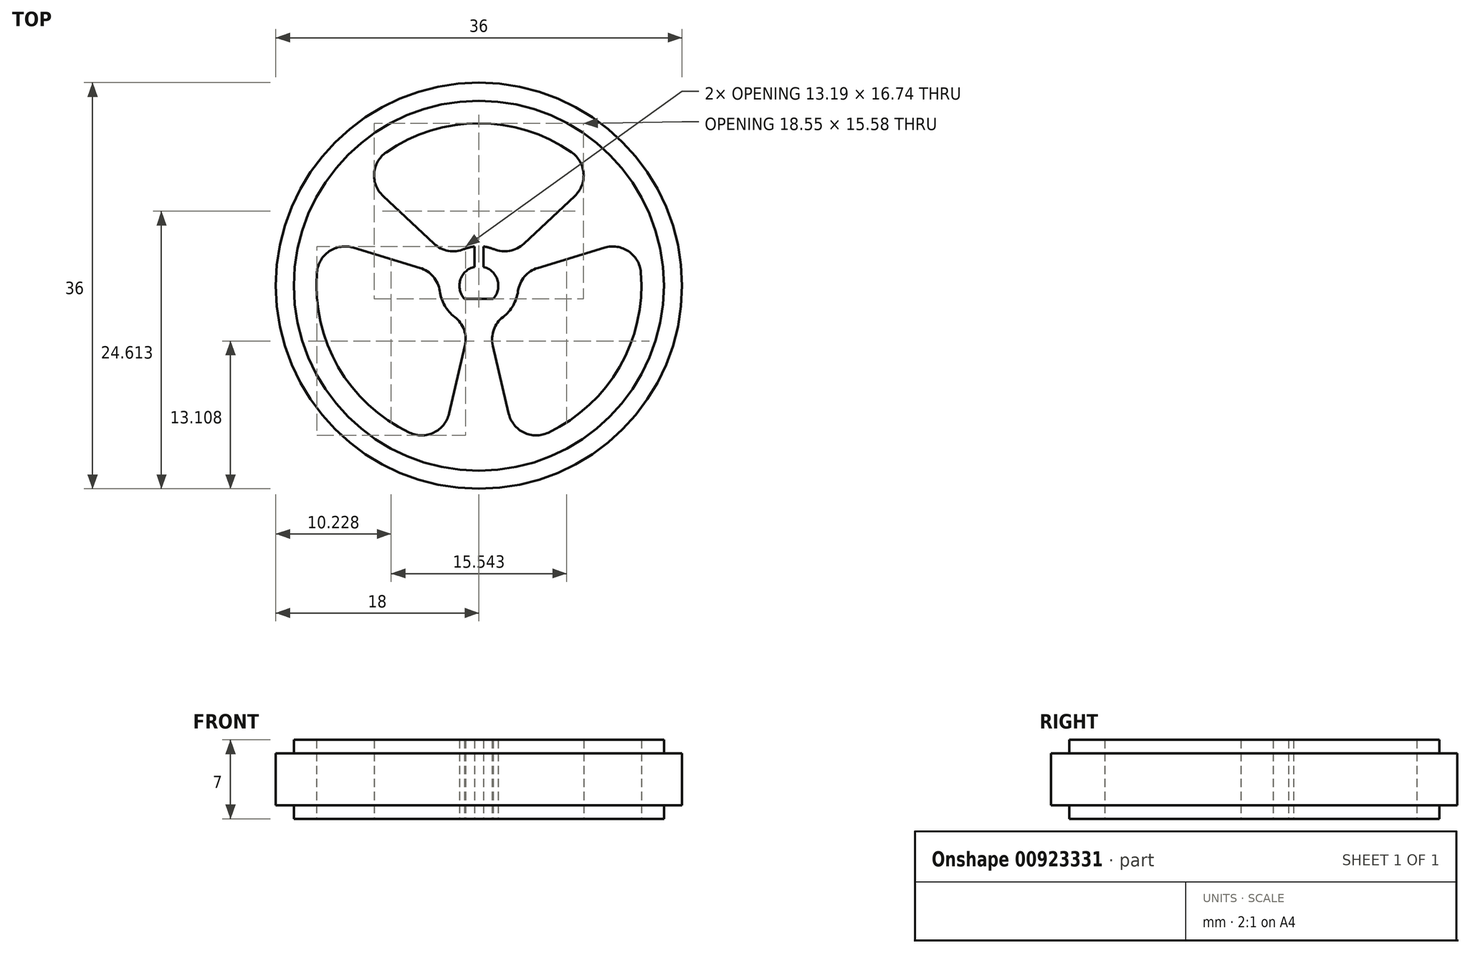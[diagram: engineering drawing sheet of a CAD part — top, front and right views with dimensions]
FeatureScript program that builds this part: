
annotation { "Feature Type Name" : "Feature", "Feature Type Description" : "" }
export const myFeature = defineFeature(function(context is Context, id is Id, definition is map)
    precondition{}
    {
        {
            var Q0;
            Q0=qCreatedBy(makeId("Front.planeOp"),FACE);
            var sketch = newSketch(context, id + "F0", { "sketchPlane" : qUnion([Q0])});
            skLineSegment(sketch, "E0", {"start": v(0, 0) * mm, "end": v(-16.4, 0) * mm});
            skLineSegment(sketch, "E1", {"start": v(-16.4, 0) * mm, "end": v(-16.4, 1.2) * mm});
            skLineSegment(sketch, "E2", {"start": v(-16.4, 1.2) * mm, "end": v(-18, 1.2) * mm});
            skLineSegment(sketch, "E3", {"start": v(-18, 1.2) * mm, "end": v(-18, 5.8) * mm});
            skLineSegment(sketch, "E4", {"start": v(-18, 5.8) * mm, "end": v(-16.4, 5.8) * mm});
            skLineSegment(sketch, "E5", {"start": v(-16.4, 5.8) * mm, "end": v(-16.4, 7) * mm});
            skLineSegment(sketch, "E6", {"start": v(-16.4, 7) * mm, "end": v(0, 7) * mm});
            skLineSegment(sketch, "E7", {"start": v(0, 7) * mm, "end": v(0, 0) * mm});
            skSolve(sketch);
        }
        {
            var Q0;
            Q0=makeQuery(id+"F0.imprint","IMPRINT",FACE,{"disambiguationData":[TD([[makeQuery(id+"F0.imprint","IMPRINT",EDGE,{"derivedFrom":sQuery(id+"F0.wireOp",EDGE,"E0")}),-1.0]])]});
            var Q1;
            Q1=sQuery(id+"F0.wireOp",EDGE,"E7");
            revolve(context, id + "F1", {"surfaceOperationType" : NewSurfaceOperationType.NEW, "entities" : qUnion([Q0]), "axis" : qUnion([Q1]), "revolveType" : RevolveType.FULL});
        }
        {
            var Q0;
            Q0=qCreatedBy(makeId("Top.planeOp"),FACE);
            var sketch = newSketch(context, id + "F2", { "sketchPlane" : qUnion([Q0])});
            skArc(sketch, "E8", {"start": v(-0.4, 1.68) * mm, "mid": v(0, -1.72) * mm, "end": v(0.4, 1.68) * mm});
            skLineSegment(sketch, "E9", {"start": v(-1.26, -1.17) * mm, "end": v(1.26, -1.17) * mm});
            skCircle(sketch, "E10.0", {"center": v(0, 0) * mm, "radius": 16.4 * mm});
            skCircle(sketch, "E11.0", {"center": v(0, 0) * mm, "radius": 14.4 * mm});
            skArc(sketch, "E12", {"start": v(-0.4, 3.48) * mm, "mid": v(0, -3.5) * mm, "end": v(0.4, 3.48) * mm});
            skLineSegment(sketch, "E13", {"start": v(-0.4, 1.68) * mm, "end": v(-0.4, 3.48) * mm});
            skLineSegment(sketch, "E14", {"start": v(0.4, 1.68) * mm, "end": v(0.4, 3.48) * mm});
            skLineSegment(sketch, "E15", {"start": v(-0.8, -3.4) * mm, "end": v(-3.27, -14.02) * mm});
            skLineSegment(sketch, "E16", {"start": v(0.8, -3.4) * mm, "end": v(3.27, -14.02) * mm});
            skLineSegment(sketch, "E17", {"start": v(0, -3.5) * mm, "end": v(0, -14.4) * mm, "construction": true});
            skLineSegment(sketch, "E18.1.0", {"start": v(3.35, 1.02) * mm, "end": v(13.78, 4.18) * mm});
            skLineSegment(sketch, "E18.1.1", {"start": v(2.55, 2.4) * mm, "end": v(10.51, 9.84) * mm});
            skLineSegment(sketch, "E18.2.0", {"start": v(-2.55, 2.4) * mm, "end": v(-10.51, 9.84) * mm});
            skLineSegment(sketch, "E18.2.1", {"start": v(-3.35, 1.02) * mm, "end": v(-13.78, 4.18) * mm});
            skSolve(sketch);
        }
        {
            var Q0;
            {var subQ5=sQuery(id+"F2.wireOp",EDGE,"E9");Q0=makeQuery(id+"F2.imprint","IMPRINT",FACE,{"disambiguationData":[TD([[makeQuery(id+"F2.imprint","IMPRINT",EDGE,{"derivedFrom":subQ5}),1.0]])]});}
            var Q1;
            {var subQ0=sQuery(id+"F2.wireOp",EDGE,"E16");Q1=makeQuery(id+"F2.imprint","IMPRINT",FACE,{"disambiguationData":[TD([[makeQuery(id+"F2.imprint","IMPRINT",EDGE,{"derivedFrom":subQ0}),1.0]])]});}
            var Q2;
            {var subQ0=sQuery(id+"F2.wireOp",EDGE,"E15");Q2=makeQuery(id+"F2.imprint","IMPRINT",FACE,{"disambiguationData":[TD([[makeQuery(id+"F2.imprint","IMPRINT",EDGE,{"derivedFrom":subQ0}),-1.0]])]});}
            var Q3;
            Q3=makeQuery(id+"F1.opRevolve","SWEPT_FACE",FACE,{"disambiguationData":[OSD([sQuery(id+"F0.wireOp",EDGE,"E6")])]});
            extrude(context, id + "F3", {"entities" : qUnion([Q0, Q1, Q2]), "operationType" : NewBodyOperationType.REMOVE, "endBound" : BoundingType.UP_TO_SURFACE, "depth" : 25 * mm, "endBoundEntityFace" : qUnion([Q3]), "offsetDistance" : 25 * mm});
        }
        {
            var Q0;
            Q0=makeQuery(id+"F3.boolean.opBoolean","COPY",EDGE,{"derivedFrom":makeQuery(id+"F3.opExtrude","SWEPT_EDGE",EDGE,{"disambiguationData":[OSD([sQuery(id+"F2.wireOp",EDGE,"E12"),sQuery(id+"F2.wireOp",EDGE,"E18.2.1")])]})});
            var Q1;
            Q1=makeQuery(id+"F3.boolean.opBoolean","COPY",EDGE,{"derivedFrom":makeQuery(id+"F3.opExtrude","SWEPT_EDGE",EDGE,{"disambiguationData":[OSD([sQuery(id+"F2.wireOp",EDGE,"E12"),sQuery(id+"F2.wireOp",EDGE,"E15")])]})});
            var Q2;
            Q2=makeQuery(id+"F3.boolean.opBoolean","COPY",EDGE,{"derivedFrom":makeQuery(id+"F3.opExtrude","SWEPT_EDGE",EDGE,{"disambiguationData":[OSD([sQuery(id+"F2.wireOp",EDGE,"E12"),sQuery(id+"F2.wireOp",EDGE,"E16")])]})});
            var Q3;
            Q3=makeQuery(id+"F3.boolean.opBoolean","COPY",EDGE,{"derivedFrom":makeQuery(id+"F3.opExtrude","SWEPT_EDGE",EDGE,{"disambiguationData":[OSD([sQuery(id+"F2.wireOp",EDGE,"E12"),sQuery(id+"F2.wireOp",EDGE,"E18.1.0")])]})});
            var Q4;
            Q4=makeQuery(id+"F3.boolean.opBoolean","COPY",EDGE,{"derivedFrom":makeQuery(id+"F3.opExtrude","SWEPT_EDGE",EDGE,{"disambiguationData":[OSD([sQuery(id+"F2.wireOp",EDGE,"E12"),sQuery(id+"F2.wireOp",EDGE,"E18.2.0")])]})});
            var Q5;
            Q5=makeQuery(id+"F3.boolean.opBoolean","COPY",EDGE,{"derivedFrom":makeQuery(id+"F3.opExtrude","SWEPT_EDGE",EDGE,{"disambiguationData":[OSD([sQuery(id+"F2.wireOp",EDGE,"E12"),sQuery(id+"F2.wireOp",EDGE,"E18.1.1")])]})});
            var Q6;
            Q6=makeQuery(id+"F3.boolean.opBoolean","COPY",EDGE,{"derivedFrom":makeQuery(id+"F3.opExtrude","SWEPT_EDGE",EDGE,{"disambiguationData":[OSD([sQuery(id+"F2.wireOp",EDGE,"E11.0"),sQuery(id+"F2.wireOp",EDGE,"E18.2.0")])]})});
            var Q7;
            Q7=makeQuery(id+"F3.boolean.opBoolean","COPY",EDGE,{"derivedFrom":makeQuery(id+"F3.opExtrude","SWEPT_EDGE",EDGE,{"disambiguationData":[OSD([sQuery(id+"F2.wireOp",EDGE,"E11.0"),sQuery(id+"F2.wireOp",EDGE,"E18.1.1")])]})});
            var Q8;
            Q8=makeQuery(id+"F3.boolean.opBoolean","COPY",EDGE,{"derivedFrom":makeQuery(id+"F3.opExtrude","SWEPT_EDGE",EDGE,{"disambiguationData":[OSD([sQuery(id+"F2.wireOp",EDGE,"E11.0"),sQuery(id+"F2.wireOp",EDGE,"E18.1.0")])]})});
            var Q9;
            Q9=makeQuery(id+"F3.boolean.opBoolean","COPY",EDGE,{"derivedFrom":makeQuery(id+"F3.opExtrude","SWEPT_EDGE",EDGE,{"disambiguationData":[OSD([sQuery(id+"F2.wireOp",EDGE,"E11.0"),sQuery(id+"F2.wireOp",EDGE,"E16")])]})});
            var Q10;
            Q10=makeQuery(id+"F3.boolean.opBoolean","COPY",EDGE,{"derivedFrom":makeQuery(id+"F3.opExtrude","SWEPT_EDGE",EDGE,{"disambiguationData":[OSD([sQuery(id+"F2.wireOp",EDGE,"E11.0"),sQuery(id+"F2.wireOp",EDGE,"E15")])]})});
            var Q11;
            Q11=makeQuery(id+"F3.boolean.opBoolean","COPY",EDGE,{"derivedFrom":makeQuery(id+"F3.opExtrude","SWEPT_EDGE",EDGE,{"disambiguationData":[OSD([sQuery(id+"F2.wireOp",EDGE,"E11.0"),sQuery(id+"F2.wireOp",EDGE,"E18.2.1")])]})});
            fillet(context, id + "F4", {"entities" : qUnion([Q0, Q1, Q2, Q3, Q4, Q5, Q6, Q7, Q8, Q9, Q10, Q11]), "radius" : 2.5 * mm, "tangentPropagation" : true, "defaultsChanged" : false, "vertexSettings" : [], "allowEdgeOverflow" : false});
        }
    });
